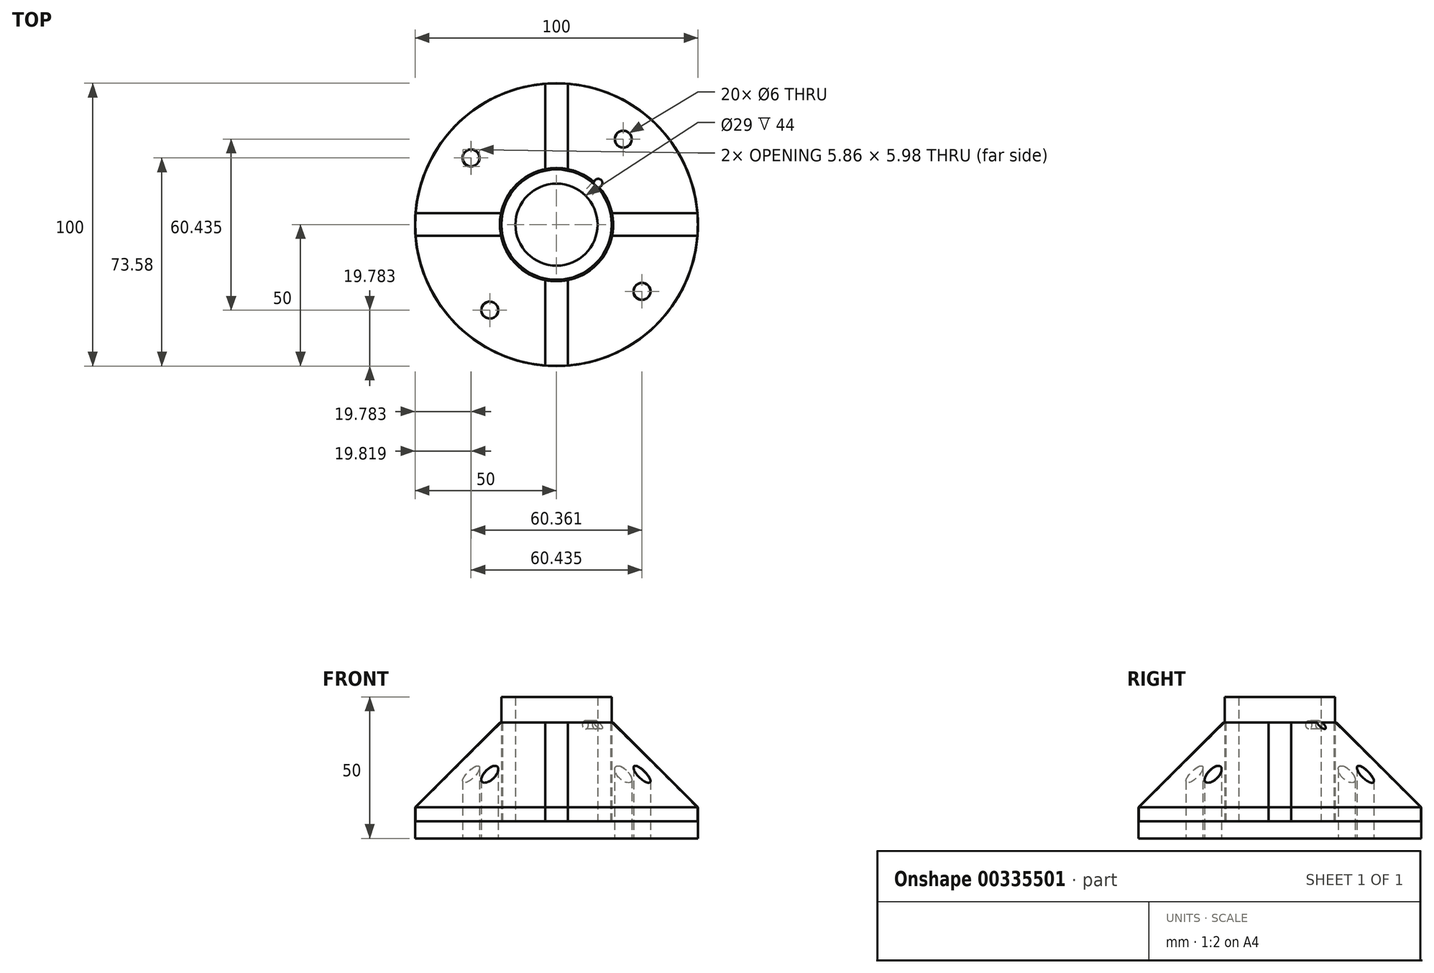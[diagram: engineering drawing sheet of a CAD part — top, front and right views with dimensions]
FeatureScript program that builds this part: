
annotation { "Feature Type Name" : "Feature", "Feature Type Description" : "" }
export const myFeature = defineFeature(function(context is Context, id is Id, definition is map)
    precondition{}
    {
        {
            var Q0;
            Q0=qCreatedBy(makeId("Top.planeOp"),FACE);
            var sketch = newSketch(context, id + "F0", { "sketchPlane" : qUnion([Q0])});
            skCircle(sketch, "E0", {"center": v(0, 0) * mm, "radius": 14.5 * mm});
            skCircle(sketch, "E1", {"center": v(0, 0) * mm, "radius": 19.5 * mm});
            skCircle(sketch, "E2", {"center": v(0, 116.74) * mm, "radius": 2 * mm});
            skLineSegment(sketch, "E3", {"start": v(10, 16.74) * mm, "end": v(10, 116.74) * mm});
            skLineSegment(sketch, "E4", {"start": v(-10, 16.74) * mm, "end": v(-10, 116.74) * mm});
            skArc(sketch, "E5", {"start": v(10, 116.74) * mm, "mid": v(0, 126.74) * mm, "end": v(-10, 116.74) * mm});
            skLineSegment(sketch, "E6", {"start": v(0, 0) * mm, "end": v(98.42, 52.33) * mm, "construction": true});
            skCircle(sketch, "E7", {"center": v(103.08, 54.8) * mm, "radius": 2 * mm});
            skLineSegment(sketch, "E8", {"start": v(10.09, 16.69) * mm, "end": v(98.38, 63.64) * mm});
            skLineSegment(sketch, "E9", {"start": v(19.48, -0.97) * mm, "end": v(107.77, 45.98) * mm});
            skArc(sketch, "E10", {"start": v(107.77, 45.98) * mm, "mid": v(111.9, 59.5) * mm, "end": v(98.38, 63.64) * mm});
            skLineSegment(sketch, "E11", {"start": v(98.38, 63.64) * mm, "end": v(107.77, 45.98) * mm, "construction": true});
            skSolve(sketch);
        }
        {
            var Q0;
            Q0=makeQuery(id+"F0.imprint","IMPRINT",FACE,{"disambiguationData":[TD([[makeQuery(id+"F0.imprint","IMPRINT",EDGE,{"derivedFrom":sQuery(id+"F0.wireOp",EDGE,"E0")}),-1.0]])]});
            extrude(context, id + "F1", {"entities" : qUnion([Q0]), "depth" : 50 * mm, "offsetDistance" : 25 * mm});
        }
        {
            var Q0;
            Q0=makeQuery(id+"F0.imprint","IMPRINT",FACE,{"disambiguationData":[TD([[makeQuery(id+"F0.imprint","IMPRINT",EDGE,{"derivedFrom":sQuery(id+"F0.wireOp",EDGE,"E0")}),1.0]])]});
            extrude(context, id + "F2", {"entities" : qUnion([Q0]), "operationType" : NewBodyOperationType.ADD, "depth" : 2 * mm, "offsetDistance" : 25 * mm});
        }
        {
            var Q0;
            Q0=qCreatedBy(makeId("Top.planeOp"),FACE);
            var sketch = newSketch(context, id + "F3", { "sketchPlane" : qUnion([Q0])});
            skCircle(sketch, "E12", {"center": v(0, 0) * mm, "radius": 50 * mm});
            skCircle(sketch, "E13", {"center": v(-30.22, 23.6) * mm, "radius": 3 * mm});
            skCircle(sketch, "E14.1.0", {"center": v(-23.6, -30.22) * mm, "radius": 3 * mm});
            skCircle(sketch, "E14.2.0", {"center": v(30.22, -23.6) * mm, "radius": 3 * mm});
            skCircle(sketch, "E15.1.3.0", {"center": v(23.6, 30.22) * mm, "radius": 3 * mm});
            skSolve(sketch);
        }
        {
            var Q0;
            Q0=makeQuery(id+"F3.imprint","IMPRINT",FACE,{"disambiguationData":[TD([[makeQuery(id+"F3.imprint","IMPRINT",EDGE,{"derivedFrom":sQuery(id+"F3.wireOp",EDGE,"E12")}),1.0]])]});
            extrude(context, id + "F4", {"entities" : qUnion([Q0]), "operationType" : NewBodyOperationType.ADD, "depth" : 6 * mm, "offsetDistance" : 25 * mm});
        }
        {
            var Q0;
            {var subQ0=sQuery(id+"F3.wireOp",EDGE,"E14.1.0");var subQ1=sQuery(id+"F3.wireOp",EDGE,"E12");var subQ2=sQuery(id+"F3.wireOp",EDGE,"E13");var subQ3=sQuery(id+"F3.wireOp",EDGE,"E14.2.0");var subQ4=sQuery(id+"F3.wireOp",EDGE,"E15.1.3.0");Q0=makeQuery(id+"F4.boolean.opBoolean","SPLIT",FACE,{"disambiguationData":[TD([makeQuery(id+"F1.opExtrude","SWEPT_FACE",FACE,{"disambiguationData":[OSD([sQuery(id+"F0.wireOp",EDGE,"E1")])]})])],"derivedFrom":makeQuery(id+"F4.opExtrude","CAP_FACE",FACE,{"disambiguationData":[OSD([subQ1,subQ2,subQ0,subQ3,subQ4])],"isStart":false})});}
            var sketch = newSketch(context, id + "F5", { "sketchPlane" : qUnion([Q0])});
            skCircle(sketch, "E16.0", {"center": v(0, 0) * mm, "radius": 50 * mm});
            skCircle(sketch, "E16.1", {"center": v(0, 0) * mm, "radius": 19.5 * mm});
            skLineSegment(sketch, "E17", {"start": v(-4, 49.84) * mm, "end": v(-4, 16.6) * mm});
            skLineSegment(sketch, "E18", {"start": v(-4, 16.6) * mm, "end": v(4, 16.6) * mm});
            skLineSegment(sketch, "E19", {"start": v(4, 16.6) * mm, "end": v(4, 49.84) * mm});
            skArc(sketch, "E20", {"start": v(4, 49.84) * mm, "mid": v(0, 50) * mm, "end": v(-4, 49.84) * mm});
            skSolve(sketch);
        }
        {
            var Q0;
            {var subQ0=sQuery(id+"F5.wireOp",EDGE,"E17");var subQ1=sQuery(id+"F5.wireOp",EDGE,"E16.0");var subQ2=makeQuery(id+"F5.imprint","INTERSECT",VERTEX,{"derivedFrom":[subQ1,subQ0]});Q0=makeQuery(id+"F5.imprint","IMPRINT",FACE,{"disambiguationData":[TD([[makeQuery(id+"F5.imprint","IMPRINT",EDGE,{"disambiguationData":[TD([[subQ2,1.0]])],"derivedFrom":subQ1}),1.0]])]});}
            extrude(context, id + "F6", {"entities" : qUnion([Q0]), "depth" : 35 * mm, "offsetDistance" : 25 * mm});
        }
        {
            var Q0;
            Q0=makeQuery(id+"F6.opExtrude","CAP_EDGE",EDGE,{"disambiguationData":[OSD([sQuery(id+"F5.wireOp",EDGE,"E16.0")])],"isStart":false});
            chamfer(context, id + "F7", {"entities" : qUnion([Q0]), "width" : 30 * mm, "tangentPropagation" : true});
        }
        {
            var Q0;
            Q0=makeQuery(id+"F6.opExtrude","SWEPT_BODY",BODY,{"disambiguationData":[OSD([sQuery(id+"F5.wireOp",EDGE,"E16.0"),sQuery(id+"F5.wireOp",EDGE,"E16.1"),sQuery(id+"F5.wireOp",EDGE,"E17"),sQuery(id+"F5.wireOp",EDGE,"E19")])]});
            var Q1;
            Q1=makeQuery(id+"F1.opExtrude","SWEPT_FACE",FACE,{"disambiguationData":[OSD([sQuery(id+"F0.wireOp",EDGE,"E0")])]});
            circularPattern(context, id + "F8", {"entities" : qUnion([Q0]), "axis" : qUnion([Q1]), "angle" : 360 * degree, "instanceCount" : 4, "equalSpace" : true});
        }
        {
            var Q0;
            Q0=qCreatedBy(makeId("Right.planeOp"),FACE);
            var Q1;
            Q1=makeQuery(id+"F1.opExtrude","SWEPT_FACE",FACE,{"disambiguationData":[OSD([sQuery(id+"F0.wireOp",EDGE,"E0")])]});
            cPlane(context, id + "F9", {"entities" : qUnion([Q0, Q1]), "cplaneType" : CPlaneType.LINE_ANGLE, "offset" : 25 * mm, "angle" : 45 * degree, "width" : 150 * mm, "height" : 150 * mm});
        }
        {
            var Q0;
            Q0=qCreatedBy(id+"F9.planeOp",FACE);
            var sketch = newSketch(context, id + "F10", { "sketchPlane" : qUnion([Q0])});
            skCircle(sketch, "E21", {"center": v(0, 40.16) * mm, "radius": 1.5 * mm});
            skSolve(sketch);
        }
        {
            var Q0;
            Q0=makeQuery(id+"F10.imprint","IMPRINT",FACE,{"disambiguationData":[TD([[makeQuery(id+"F10.imprint","IMPRINT",EDGE,{"derivedFrom":sQuery(id+"F10.wireOp",EDGE,"E21")}),1.0]])]});
            extrude(context, id + "F11", {"entities" : qUnion([Q0]), "operationType" : NewBodyOperationType.REMOVE, "oppositeDirection" : true, "depth" : 30 * mm, "offsetDistance" : 25 * mm});
        }
    });
